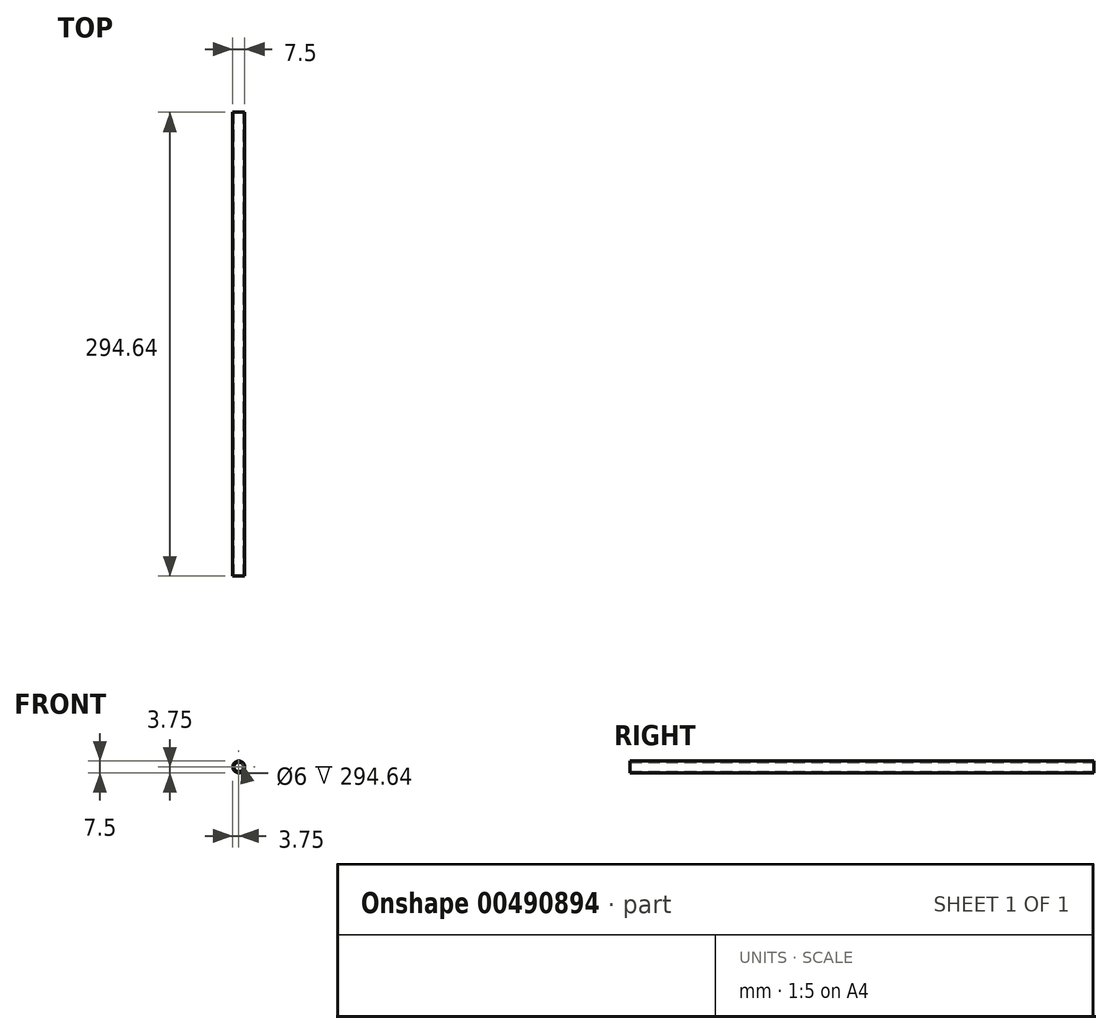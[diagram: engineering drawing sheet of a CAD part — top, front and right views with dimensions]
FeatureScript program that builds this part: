
annotation { "Feature Type Name" : "Feature", "Feature Type Description" : "" }
export const myFeature = defineFeature(function(context is Context, id is Id, definition is map)
    precondition{}
    {
        {
            var Q0;
            Q0=qCreatedBy(makeId("Front.planeOp"),FACE);
            var sketch = newSketch(context, id + "F0", { "sketchPlane" : qUnion([Q0])});
            skCircle(sketch, "E0", {"center": v(0, 0) * mm, "radius": 3.75 * mm});
            skCircle(sketch, "E1", {"center": v(0, 0) * mm, "radius": 3 * mm});
            skSolve(sketch);
        }
        {
            var Q0;
            Q0=makeQuery(id+"F0.imprint","IMPRINT",FACE,{"disambiguationData":[TD([[makeQuery(id+"F0.imprint","IMPRINT",EDGE,{"derivedFrom":sQuery(id+"F0.wireOp",EDGE,"E0")}),1.0]])]});
            extrude(context, id + "F1", {"entities" : qUnion([Q0]), "depth" : 294.64 * mm, "offsetDistance" : 25.4 * mm});
        }
    });
